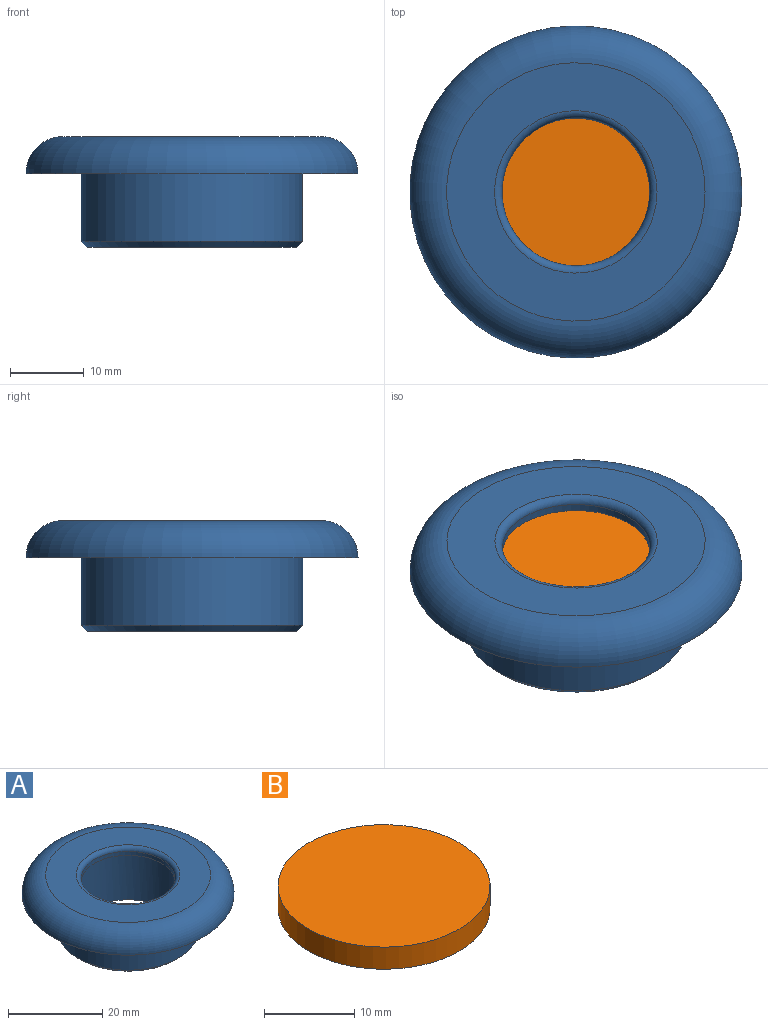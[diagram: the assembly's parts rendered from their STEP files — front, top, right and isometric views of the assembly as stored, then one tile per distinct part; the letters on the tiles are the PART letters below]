
ASSEMBLY  parts=2 mates=1
PART A: 10 faces, bbox 48.7x48.7x15 mm
  f0: cylinder r=10mm len=20mm, axis (0,0,1), area 62.8mm2, adj f7,f9
  f1: cylinder r=15mm len=30mm, axis (0,0,-1), area 867.1mm2, adj f3,f5
  f2: plane 28.4x28.4mm, normal (0,0,-1), area 181.1mm2, adj f3,f4
  f3: cone r=15mm half-angle=45deg, axis (0,0,1), area 103.8mm2, adj f1,f2
  f4: cylinder r=12mm len=24mm, axis (0,0,-1), area 980.2mm2, adj f2,f9
  f5: plane 45x45mm, normal (0,0,-1), area 883.6mm2, adj f1,f8
  f6: plane 35x35mm, normal (0,0,1), area 582mm2, adj f7,f8
  f7: torus R=11mm, axis (0,0,1), area 102.3mm2, adj f0,f6
  f8: torus R=17.5mm, axis (0,0,1), area 1020.7mm2, adj f5,f6
  f9: plane 24x24mm, normal (0,0,-1), area 138.2mm2, adj f0,f4
PART B: 3 faces, bbox 23.5x23.5x3 mm
  f0: cylinder r=11.75mm len=23.5mm, axis (0,0,-1), area 221.5mm2, adj f1,f2
  f1: plane 23.5x23.5mm, normal (0,0,1), area 433.7mm2, adj f0
  f2: plane 23.5x23.5mm, normal (0,0,-1), area 433.7mm2, adj f0
PLACE A t=(-8.44,-1.71,-2.75)mm
PLACE B t=(-8.44,-1.71,7.25)mm
MATE cylindrical B.f0 <-> A.f4  axis (0,0,1) through (-8.44,-1.71,10.25)mm
